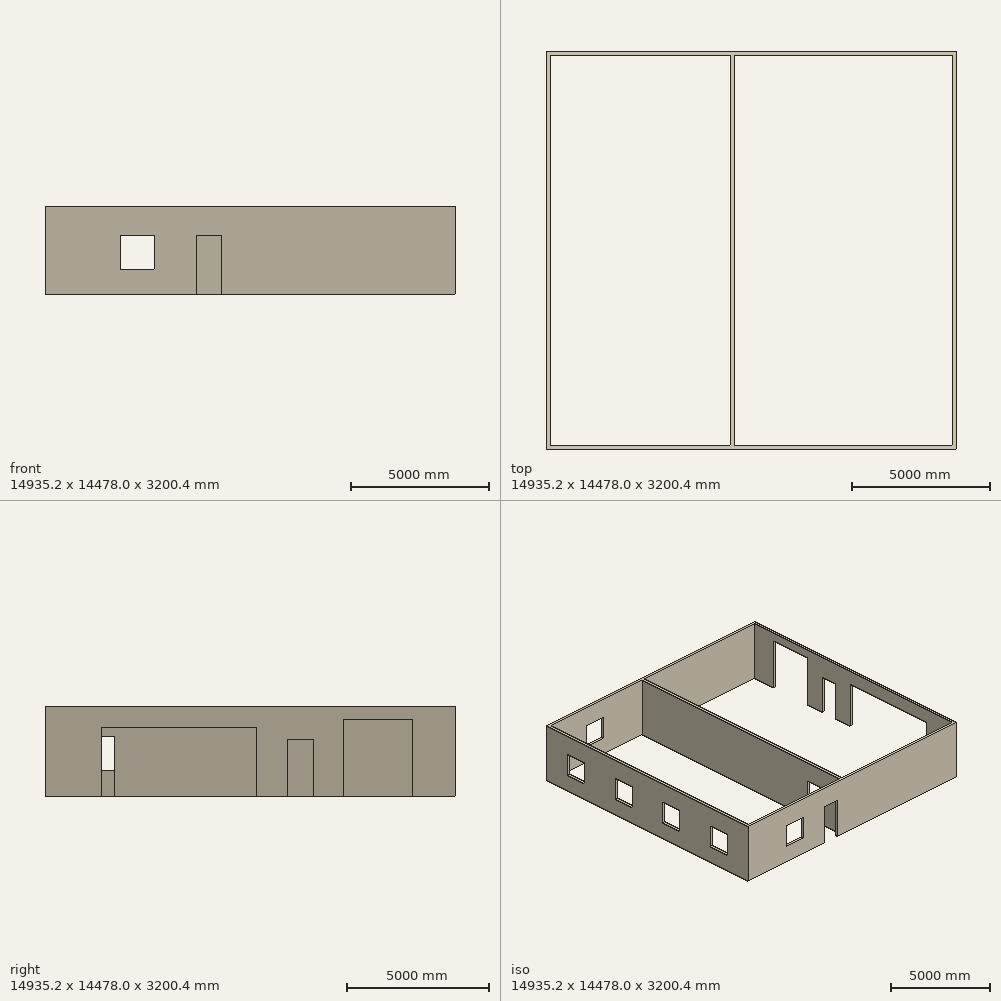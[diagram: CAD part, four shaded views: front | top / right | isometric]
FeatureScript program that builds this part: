
annotation { "Feature Type Name" : "Feature", "Feature Type Description" : "" }
export const myFeature = defineFeature(function(context is Context, id is Id, definition is map)
    precondition{}
    {
        {
            var Q0;
            Q0=qCreatedBy(makeId("Top.planeOp"),FACE);
            var sketch = newSketch(context, id + "F0", { "sketchPlane" : qUnion([Q0])});
            skLineSegment(sketch, "E0.bottom", {"start": v(-7467.6, 7239) * mm, "end": v(7467.6, 7239) * mm});
            skLineSegment(sketch, "E0.top", {"start": v(-7467.6, -7239) * mm, "end": v(7467.6, -7239) * mm});
            skLineSegment(sketch, "E0.left", {"start": v(-7467.6, 7239) * mm, "end": v(-7467.6, -7239) * mm});
            skLineSegment(sketch, "E0.right", {"start": v(7467.6, 7239) * mm, "end": v(7467.6, -7239) * mm});
            skSolve(sketch);
        }
        {
            var Q0;
            Q0=makeQuery(id+"F0.imprint","IMPRINT",FACE,{"disambiguationData":[TD([[makeQuery(id+"F0.imprint","IMPRINT",EDGE,{"derivedFrom":sQuery(id+"F0.wireOp",EDGE,"E0.bottom")}),-1.0]])]});
            var Q1;
            Q1 = qConstructionFilter(qBodyType(qCreatedBy(id + "F0" ,EDGE), BodyType.WIRE), ConstructionObject.NO);
            extrude(context, id + "F1", {"entities" : qUnion([Q0]), "surfaceEntities" : qUnion([Q1]), "oppositeDirection" : true, "depth" : 3200.4 * mm});
        }
        {
            var Q0;
            Q0=makeQuery(id+"F1.opExtrude","CAP_FACE",FACE,{"disambiguationData":[OSD([sQuery(id+"F0.wireOp",EDGE,"E0.bottom"),sQuery(id+"F0.wireOp",EDGE,"E0.top"),sQuery(id+"F0.wireOp",EDGE,"E0.left"),sQuery(id+"F0.wireOp",EDGE,"E0.right")])],"isStart":true});
            var Q1;
            Q1=makeQuery(id+"F1.opExtrude","CAP_FACE",FACE,{"disambiguationData":[OSD([sQuery(id+"F0.wireOp",EDGE,"E0.bottom"),sQuery(id+"F0.wireOp",EDGE,"E0.top"),sQuery(id+"F0.wireOp",EDGE,"E0.left"),sQuery(id+"F0.wireOp",EDGE,"E0.right")])],"isStart":false});
            shell(context, id + "F2", {"entities" : qUnion([Q0, Q1]), "thickness" : 152.4 * mm});
        }
        {
            var Q0;
            Q0=makeQuery(id+"F1.opExtrude","SWEPT_FACE",FACE,{"disambiguationData":[OSD([sQuery(id+"F0.wireOp",EDGE,"E0.right")])]});
            var sketch = newSketch(context, id + "F3", { "sketchPlane" : qUnion([Q0])});
            skLineSegment(sketch, "E1.bottom", {"start": v(-5257.8, -3200.4) * mm, "end": v(228.6, -3200.4) * mm});
            skLineSegment(sketch, "E1.top", {"start": v(-5257.8, -762) * mm, "end": v(228.6, -762) * mm});
            skLineSegment(sketch, "E1.left", {"start": v(-5257.8, -3200.4) * mm, "end": v(-5257.8, -762) * mm});
            skLineSegment(sketch, "E1.right", {"start": v(228.6, -3200.4) * mm, "end": v(228.6, -762) * mm});
            skSolve(sketch);
        }
        {
            var Q0;
            Q0 = qSketchRegion(id + "F3", true);
            extrude(context, id + "F4", {"entities" : qUnion([Q0]), "operationType" : NewBodyOperationType.REMOVE, "endBound" : BoundingType.UP_TO_NEXT, "oppositeDirection" : true, "depth" : 30.48 * mm});
        }
        {
            var Q0;
            Q0=makeQuery(id+"F1.opExtrude","SWEPT_FACE",FACE,{"disambiguationData":[OSD([sQuery(id+"F0.wireOp",EDGE,"E0.right")])]});
            var sketch = newSketch(context, id + "F5", { "sketchPlane" : qUnion([Q0])});
            skLineSegment(sketch, "E2.bottom", {"start": v(3276.6, -3200.4) * mm, "end": v(5715, -3200.4) * mm});
            skLineSegment(sketch, "E2.top", {"start": v(3276.6, -457.2) * mm, "end": v(5715, -457.2) * mm});
            skLineSegment(sketch, "E2.left", {"start": v(3276.6, -3200.4) * mm, "end": v(3276.6, -457.2) * mm});
            skLineSegment(sketch, "E2.right", {"start": v(5715, -3200.4) * mm, "end": v(5715, -457.2) * mm});
            skSolve(sketch);
        }
        {
            var Q0;
            Q0 = qSketchRegion(id + "F5", true);
            extrude(context, id + "F6", {"entities" : qUnion([Q0]), "operationType" : NewBodyOperationType.REMOVE, "endBound" : BoundingType.UP_TO_NEXT, "oppositeDirection" : true, "depth" : 30.48 * mm});
        }
        {
            var Q0;
            Q0=makeQuery(id+"F1.opExtrude","SWEPT_FACE",FACE,{"disambiguationData":[OSD([sQuery(id+"F0.wireOp",EDGE,"E0.right")])]});
            var sketch = newSketch(context, id + "F7", { "sketchPlane" : qUnion([Q0])});
            skLineSegment(sketch, "E3.bottom", {"start": v(1295.4, -3200.4) * mm, "end": v(2209.8, -3200.4) * mm});
            skLineSegment(sketch, "E3.top", {"start": v(1295.4, -1168.4) * mm, "end": v(2209.8, -1168.4) * mm});
            skLineSegment(sketch, "E3.left", {"start": v(1295.4, -3200.4) * mm, "end": v(1295.4, -1168.4) * mm});
            skLineSegment(sketch, "E3.right", {"start": v(2209.8, -3200.4) * mm, "end": v(2209.8, -1168.4) * mm});
            skSolve(sketch);
        }
        {
            var Q0;
            Q0 = qSketchRegion(id + "F7", true);
            extrude(context, id + "F8", {"entities" : qUnion([Q0]), "operationType" : NewBodyOperationType.REMOVE, "endBound" : BoundingType.UP_TO_NEXT, "oppositeDirection" : true, "depth" : 30.48 * mm});
        }
        {
            var Q0;
            Q0=makeQuery(id+"F0.imprint","IMPRINT",FACE,{"disambiguationData":[TD([[makeQuery(id+"F0.imprint","IMPRINT",EDGE,{"derivedFrom":sQuery(id+"F0.wireOp",EDGE,"E0.bottom")}),-1.0]])]});
            var sketch = newSketch(context, id + "F9", { "sketchPlane" : qUnion([Q0])});
            skLineSegment(sketch, "E4.bottom", {"start": v(-762, 7086.6) * mm, "end": v(-609.6, 7086.6) * mm});
            skLineSegment(sketch, "E4.top", {"start": v(-762, -7086.6) * mm, "end": v(-609.6, -7086.6) * mm});
            skLineSegment(sketch, "E4.left", {"start": v(-762, 7086.6) * mm, "end": v(-762, -7086.6) * mm});
            skLineSegment(sketch, "E4.right", {"start": v(-609.6, 7086.6) * mm, "end": v(-609.6, -7086.6) * mm});
            skSolve(sketch);
        }
        {
            var Q0;
            Q0 = qSketchRegion(id + "F9", true);
            var Q1;
            Q1=makeQuery(id+"F1.opExtrude","CAP_FACE",FACE,{"disambiguationData":[OSD([sQuery(id+"F0.wireOp",EDGE,"E0.bottom"),sQuery(id+"F0.wireOp",EDGE,"E0.top"),sQuery(id+"F0.wireOp",EDGE,"E0.left"),sQuery(id+"F0.wireOp",EDGE,"E0.right")])],"isStart":false});
            extrude(context, id + "F10", {"entities" : qUnion([Q0]), "operationType" : NewBodyOperationType.ADD, "endBound" : BoundingType.UP_TO_SURFACE, "oppositeDirection" : true, "endBoundEntityFace" : qUnion([Q1]), "depth" : 30.48 * mm});
        }
        {
            var Q0;
            Q0=makeQuery(id+"F1.opExtrude","SWEPT_FACE",FACE,{"disambiguationData":[OSD([sQuery(id+"F0.wireOp",EDGE,"E0.top")])]});
            var sketch = newSketch(context, id + "F11", { "sketchPlane" : qUnion([Q0])});
            skLineSegment(sketch, "E5.bottom", {"start": v(-1981.2, -3200.4) * mm, "end": v(-1066.8, -3200.4) * mm});
            skLineSegment(sketch, "E5.top", {"start": v(-1981.2, -1066.8) * mm, "end": v(-1066.8, -1066.8) * mm});
            skLineSegment(sketch, "E5.left", {"start": v(-1981.2, -3200.4) * mm, "end": v(-1981.2, -1066.8) * mm});
            skLineSegment(sketch, "E5.right", {"start": v(-1066.8, -3200.4) * mm, "end": v(-1066.8, -1066.8) * mm});
            skSolve(sketch);
        }
        {
            var Q0;
            Q0 = qSketchRegion(id + "F11", true);
            extrude(context, id + "F12", {"entities" : qUnion([Q0]), "operationType" : NewBodyOperationType.REMOVE, "endBound" : BoundingType.UP_TO_NEXT, "oppositeDirection" : true, "depth" : 30.48 * mm});
        }
        {
            var Q0;
            {var subQ3=sQuery(id+"F9.wireOp",EDGE,"E4.right");var subQ8=sQuery(id+"F0.wireOp",EDGE,"E0.top");Q0=makeQuery(id+"FsZ9RdP7XCEhl72_1.boolean.opBoolean","SPLIT",FACE,{"disambiguationData":[TD([makeQuery(id+"F2.opShell","OFFSET_FACE",FACE,{"disambiguationData":[OSD([subQ8])]})])],"derivedFrom":makeQuery(id+"F10.opExtrude","SWEPT_FACE",FACE,{"disambiguationData":[OSD([subQ3])]})});}
            var sketch = newSketch(context, id + "F13", { "sketchPlane" : qUnion([Q0])});
            skLineSegment(sketch, "E6.bottom", {"start": v(-5715, -3200.4) * mm, "end": v(-4800.6, -3200.4) * mm});
            skLineSegment(sketch, "E6.top", {"start": v(-5715, -1066.8) * mm, "end": v(-4800.6, -1066.8) * mm});
            skLineSegment(sketch, "E6.left", {"start": v(-5715, -3200.4) * mm, "end": v(-5715, -1066.8) * mm});
            skLineSegment(sketch, "E6.right", {"start": v(-4800.6, -3200.4) * mm, "end": v(-4800.6, -1066.8) * mm});
            skSolve(sketch);
        }
        {
            var Q0;
            Q0 = qSketchRegion(id + "F13", true);
            extrude(context, id + "F14", {"entities" : qUnion([Q0]), "operationType" : NewBodyOperationType.REMOVE, "endBound" : BoundingType.UP_TO_NEXT, "oppositeDirection" : true, "depth" : 637.03 * mm});
        }
        {
            var Q0;
            Q0=makeQuery(id+"F11.imprint","IMPRINT",FACE,{"disambiguationData":[TD([[makeQuery(id+"F11.imprint","IMPRINT",EDGE,{"derivedFrom":sQuery(id+"F11.wireOp",EDGE,"E5.top")}),1.0]])]});
            var sketch = newSketch(context, id + "F15", { "sketchPlane" : qUnion([Q0])});
            skLineSegment(sketch, "E7.bottom", {"start": v(-4724.4, -1066.8) * mm, "end": v(-3505.2, -1066.8) * mm});
            skLineSegment(sketch, "E7.top", {"start": v(-4724.4, -2286) * mm, "end": v(-3505.2, -2286) * mm});
            skLineSegment(sketch, "E7.left", {"start": v(-4724.4, -1066.8) * mm, "end": v(-4724.4, -2286) * mm});
            skLineSegment(sketch, "E7.right", {"start": v(-3505.2, -1066.8) * mm, "end": v(-3505.2, -2286) * mm});
            skSolve(sketch);
        }
        {
            var Q0;
            Q0 = qSketchRegion(id + "F15", true);
            extrude(context, id + "F16", {"entities" : qUnion([Q0]), "operationType" : NewBodyOperationType.REMOVE, "endBound" : BoundingType.UP_TO_NEXT, "oppositeDirection" : true, "depth" : 30.48 * mm});
        }
        {
            var Q0;
            Q0=makeQuery(id+"F1.opExtrude","SWEPT_FACE",FACE,{"disambiguationData":[OSD([sQuery(id+"F0.wireOp",EDGE,"E0.bottom")])]});
            var sketch = newSketch(context, id + "F17", { "sketchPlane" : qUnion([Q0])});
            skLineSegment(sketch, "E8.bottom", {"start": v(3505.2, -1066.8) * mm, "end": v(4724.4, -1066.8) * mm});
            skLineSegment(sketch, "E8.top", {"start": v(3505.2, -2286) * mm, "end": v(4724.4, -2286) * mm});
            skLineSegment(sketch, "E8.left", {"start": v(3505.2, -1066.8) * mm, "end": v(3505.2, -2286) * mm});
            skLineSegment(sketch, "E8.right", {"start": v(4724.4, -1066.8) * mm, "end": v(4724.4, -2286) * mm});
            skSolve(sketch);
        }
        {
            var Q0;
            Q0 = qSketchRegion(id + "F17", true);
            extrude(context, id + "F18", {"entities" : qUnion([Q0]), "operationType" : NewBodyOperationType.REMOVE, "endBound" : BoundingType.UP_TO_NEXT, "oppositeDirection" : true, "depth" : 30.48 * mm});
        }
        {
            var Q0;
            Q0=makeQuery(id+"F1.opExtrude","SWEPT_FACE",FACE,{"disambiguationData":[OSD([sQuery(id+"F0.wireOp",EDGE,"E0.left")])]});
            var sketch = newSketch(context, id + "F19", { "sketchPlane" : qUnion([Q0])});
            skLineSegment(sketch, "E9.bottom", {"start": v(-5715, -1066.8) * mm, "end": v(-4495.8, -1066.8) * mm});
            skLineSegment(sketch, "E9.top", {"start": v(-5715, -2286) * mm, "end": v(-4495.8, -2286) * mm});
            skLineSegment(sketch, "E9.left", {"start": v(-5715, -1066.8) * mm, "end": v(-5715, -2286) * mm});
            skLineSegment(sketch, "E9.right", {"start": v(-4495.8, -1066.8) * mm, "end": v(-4495.8, -2286) * mm});
            skLineSegment(sketch, "E10.bottom", {"start": v(-2311.4, -1066.8) * mm, "end": v(-1092.2, -1066.8) * mm});
            skLineSegment(sketch, "E10.top", {"start": v(-2311.4, -2286) * mm, "end": v(-1092.2, -2286) * mm});
            skLineSegment(sketch, "E10.left", {"start": v(-2311.4, -1066.8) * mm, "end": v(-2311.4, -2286) * mm});
            skLineSegment(sketch, "E10.right", {"start": v(-1092.2, -1066.8) * mm, "end": v(-1092.2, -2286) * mm});
            skLineSegment(sketch, "E11.bottom", {"start": v(1092.3, -1066.8) * mm, "end": v(2311.5, -1066.8) * mm});
            skLineSegment(sketch, "E11.top", {"start": v(1092.3, -2286) * mm, "end": v(2311.5, -2286) * mm});
            skLineSegment(sketch, "E11.left", {"start": v(1092.3, -1066.8) * mm, "end": v(1092.3, -2286) * mm});
            skLineSegment(sketch, "E11.right", {"start": v(2311.5, -1066.8) * mm, "end": v(2311.5, -2286) * mm});
            skLineSegment(sketch, "E12.bottom", {"start": v(4496, -1066.8) * mm, "end": v(5715.2, -1066.8) * mm});
            skLineSegment(sketch, "E12.top", {"start": v(4496, -2286) * mm, "end": v(5715.2, -2286) * mm});
            skLineSegment(sketch, "E12.left", {"start": v(4496, -1066.8) * mm, "end": v(4496, -2286) * mm});
            skLineSegment(sketch, "E12.right", {"start": v(5715.2, -1066.8) * mm, "end": v(5715.2, -2286) * mm});
            skSolve(sketch);
        }
        {
            var Q0;
            Q0 = qSketchRegion(id + "F19", true);
            extrude(context, id + "F20", {"entities" : qUnion([Q0]), "operationType" : NewBodyOperationType.REMOVE, "endBound" : BoundingType.UP_TO_NEXT, "oppositeDirection" : true, "depth" : 30.48 * mm});
        }
    });
